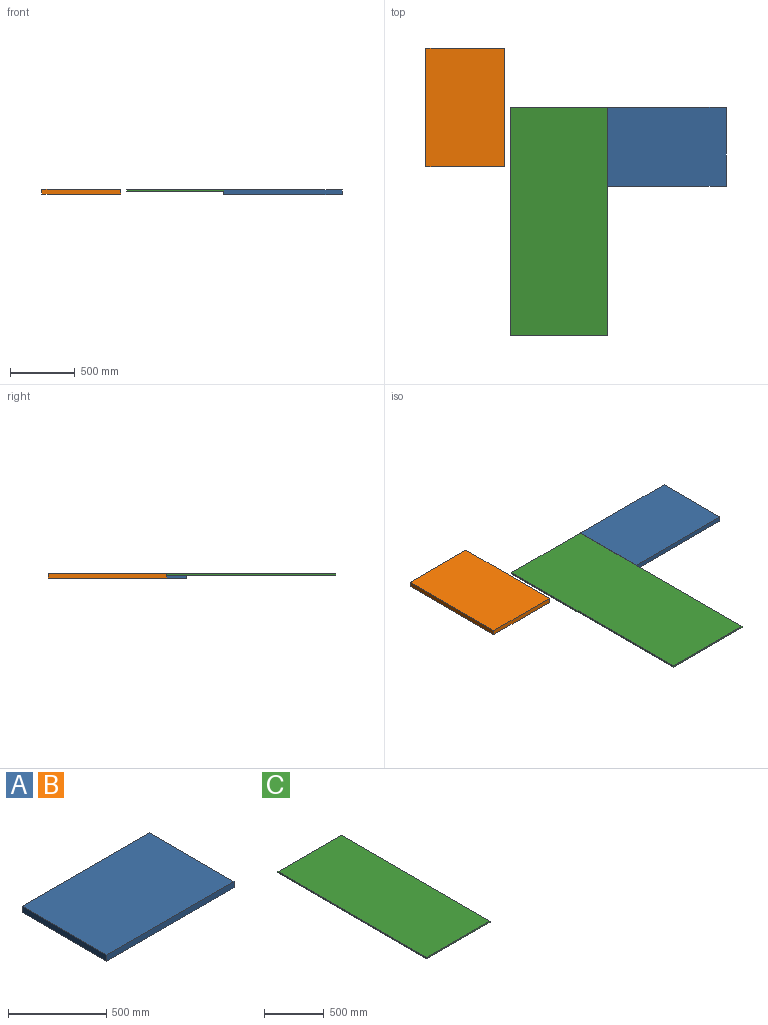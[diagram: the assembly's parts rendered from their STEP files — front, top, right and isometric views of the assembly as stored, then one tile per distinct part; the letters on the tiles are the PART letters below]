
ASSEMBLY  parts=3 mates=1
PART A: 6 faces, bbox 914.4x609.6x38.1 mm
  f0: plane 914.4x38.1mm, normal (0,1,0), area 34838.6mm2, adj f1,f3,f4,f5
  f1: plane 609.6x38.1mm, normal (-1,0,0), area 23225.8mm2, adj f0,f2,f4,f5
  f2: plane 914.4x38.1mm, normal (0,-1,0), area 34838.6mm2, adj f1,f3,f4,f5
  f3: plane 609.6x38.1mm, normal (1,0,0), area 23225.8mm2, adj f0,f2,f4,f5
  f4: plane 914.4x609.6mm, normal (0,0,1), area 557418.2mm2, adj f0,f1,f2,f3
  f5: plane 914.4x609.6mm, normal (0,0,-1), area 557418.2mm2, adj f0,f1,f2,f3
PART B: same geometry as A
PART C: 6 faces, bbox 749.3x1765.3x12.7 mm
  f0: plane 749.3x12.7mm, normal (0,1,0), area 9516.1mm2, adj f1,f3,f4,f5
  f1: plane 1765.3x12.7mm, normal (-1,0,0), area 22419.3mm2, adj f0,f2,f4,f5
  f2: plane 749.3x12.7mm, normal (0,-1,0), area 9516.1mm2, adj f1,f3,f4,f5
  f3: plane 1765.3x12.7mm, normal (1,0,0), area 22419.3mm2, adj f0,f2,f4,f5
  f4: plane 1765.3x749.3mm, normal (0,0,1), area 1322739.3mm2, adj f0,f1,f2,f3
  f5: plane 1765.3x749.3mm, normal (0,0,-1), area 1322739.3mm2, adj f0,f1,f2,f3
PLACE A t=(222.32,87.27,-338.39)mm
PLACE B rot(axis=(0.71,0.71,0),180deg) t=(-907.08,-33.01,-293.25)mm
PLACE C t=(-488.24,88.29,-312.3)mm
MATE slider B.f0 <-> C.f1  axis (1,0,0) through (-907.08,88.29,-312.3)mm
